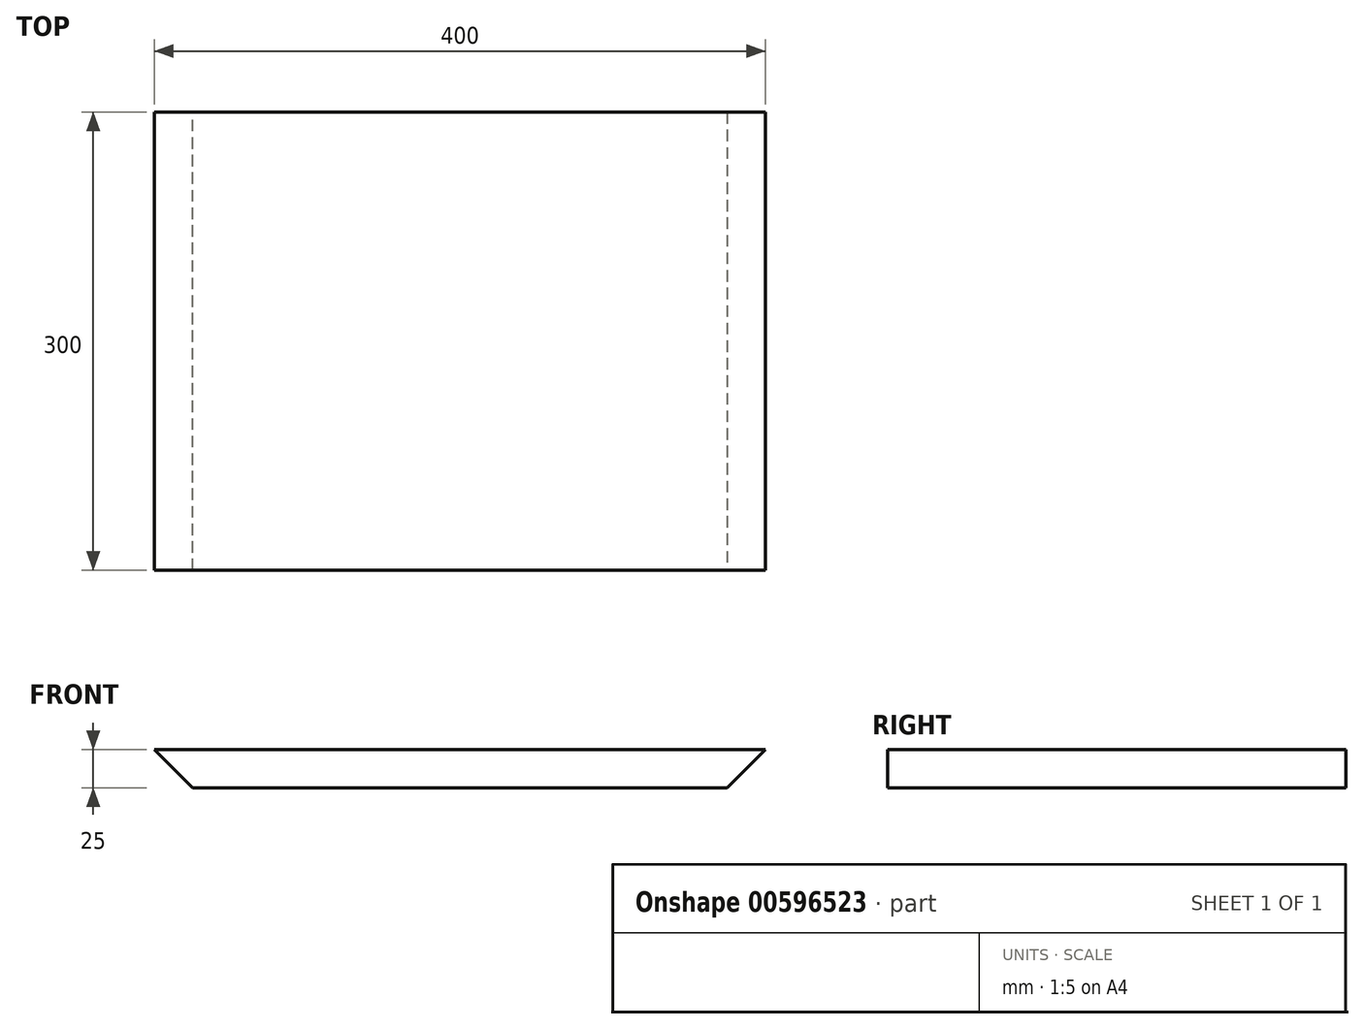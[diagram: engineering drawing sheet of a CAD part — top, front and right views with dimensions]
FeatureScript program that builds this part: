
annotation { "Feature Type Name" : "Feature", "Feature Type Description" : "" }
export const myFeature = defineFeature(function(context is Context, id is Id, definition is map)
    precondition{}
    {
        {
            var Q0;
            Q0=qCreatedBy(makeId("Top.planeOp"),FACE);
            var sketch = newSketch(context, id + "F0", { "sketchPlane" : qUnion([Q0])});
            skLineSegment(sketch, "E0.bottom", {"start": v(200, -150) * mm, "end": v(-200, -150) * mm});
            skLineSegment(sketch, "E0.top", {"start": v(200, 150) * mm, "end": v(-200, 150) * mm});
            skLineSegment(sketch, "E0.left", {"start": v(200, -150) * mm, "end": v(200, 150) * mm});
            skLineSegment(sketch, "E0.right", {"start": v(-200, -150) * mm, "end": v(-200, 150) * mm});
            skPoint(sketch, "E0.middle", {"position": v(0, 0) * mm});
            skSolve(sketch);
        }
        {
            var Q0;
            Q0=makeQuery(id+"F0.imprint","IMPRINT",FACE,{"disambiguationData":[TD([[makeQuery(id+"F0.imprint","IMPRINT",EDGE,{"derivedFrom":sQuery(id+"F0.wireOp",EDGE,"E0.bottom")}),-1.0]])]});
            extrude(context, id + "F1", {"entities" : qUnion([Q0]), "oppositeDirection" : true, "depth" : 25 * mm, "offsetDistance" : 25 * mm});
        }
        {
            var Q0;
            Q0=makeQuery(id+"F1.opExtrude","CAP_EDGE",EDGE,{"disambiguationData":[OSD([sQuery(id+"F0.wireOp",EDGE,"E0.right")])],"isStart":false});
            var Q1;
            Q1=makeQuery(id+"F1.opExtrude","CAP_EDGE",EDGE,{"disambiguationData":[OSD([sQuery(id+"F0.wireOp",EDGE,"E0.left")])],"isStart":false});
            chamfer(context, id + "F2", {"entities" : qUnion([Q0, Q1]), "width" : 25 * mm, "tangentPropagation" : true});
        }
    });
